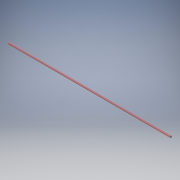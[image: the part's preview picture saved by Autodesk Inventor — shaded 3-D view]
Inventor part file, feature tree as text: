
AUTODESK INVENTOR PART (.ipt)
format: ipt  version: 2016 (Build 200138000, 138)  size: 104,960 bytes
history: native  units: mm
features: extrude x1, sketch x1
ambient origin geometry x8: Origin, YZ Plane, XZ Plane, XY Plane, X Axis, Y Axis, Z Axis, Center Point
bodies: Solid1 (feature_tree)
feature tree (2):
  extrude  "Extrusion1"  Depth=250.0mm TaperAngle=0.0deg
  sketch  "Sketch2"  dims[d0=3.0mm d1=250.0mm d2=0.0mm]
